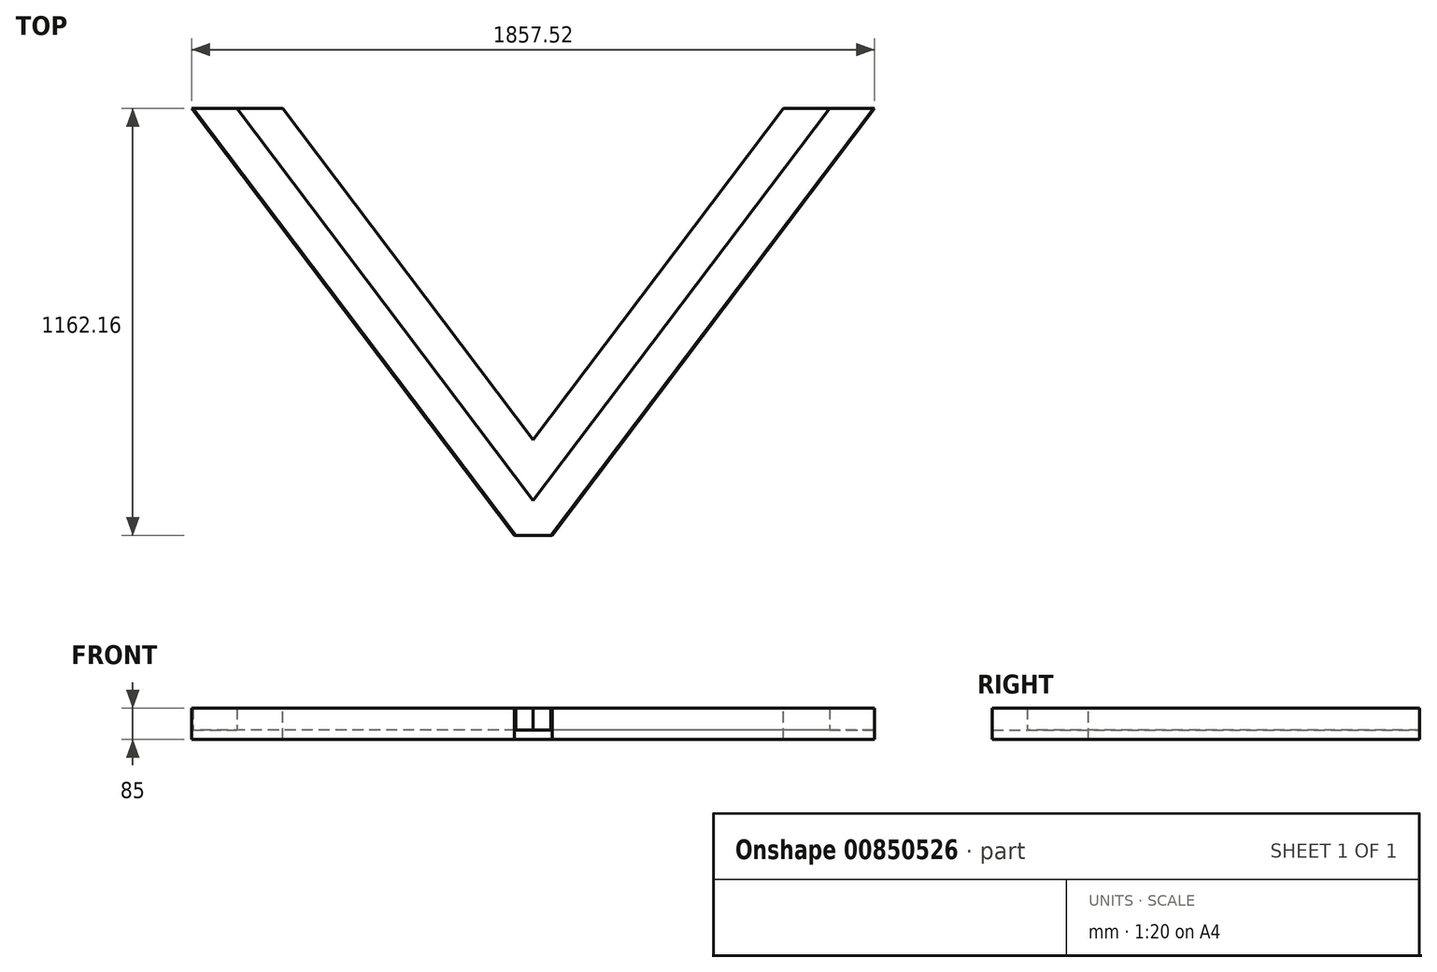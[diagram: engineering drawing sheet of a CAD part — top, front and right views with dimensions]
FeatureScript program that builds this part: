
annotation { "Feature Type Name" : "Feature", "Feature Type Description" : "" }
export const myFeature = defineFeature(function(context is Context, id is Id, definition is map)
    precondition{}
    {
        {
            var Q0;
            Q0=qCreatedBy(makeId("Top.planeOp"),FACE);
            var sketch = newSketch(context, id + "F0", { "sketchPlane" : qUnion([Q0])});
            skLineSegment(sketch, "E0", {"start": v(0, 0) * mm, "end": v(1850, 0) * mm});
            skLineSegment(sketch, "E1", {"start": v(1850, 0) * mm, "end": v(972.5, -1162.16) * mm});
            skPoint(sketch, "E1.endSnap0", {"position": v(925, 0) * mm});
            skLineSegment(sketch, "E2", {"start": v(877.5, -1162.16) * mm, "end": v(0, 0) * mm});
            skLineSegment(sketch, "E3", {"start": v(925, -1225.07) * mm, "end": v(925, -1010.6) * mm, "construction": true});
            skLineSegment(sketch, "E4", {"start": v(877.5, -1162.16) * mm, "end": v(972.5, -1162.16) * mm});
            skPoint(sketch, "E5.orphan", {"position": v(877.5, -1010.6) * mm});
            skPoint(sketch, "E6.orphan", {"position": v(972.5, -1010.6) * mm});
            skPoint(sketch, "E7.0.start.orphan", {"position": v(877.5, -1225.07) * mm});
            skPoint(sketch, "E8.MirrorCS.start.orphan", {"position": v(972.5, -1225.07) * mm});
            skSolve(sketch);
        }
        {
            var Q0;
            Q0=makeQuery(id+"F0.imprint","IMPRINT",FACE,{"disambiguationData":[TD([[makeQuery(id+"F0.imprint","IMPRINT",EDGE,{"derivedFrom":sQuery(id+"F0.wireOp",EDGE,"E0")}),-1.0]])]});
            extrude(context, id + "F1", {"entities" : qUnion([Q0]), "depth" : 25 * mm, "offsetDistance" : 25 * mm});
        }
        {
            var Q0;
            Q0=makeQuery(id+"F1.opExtrude","CAP_FACE",FACE,{"disambiguationData":[OSD([sQuery(id+"F0.wireOp",EDGE,"E0"),sQuery(id+"F0.wireOp",EDGE,"E1"),sQuery(id+"F0.wireOp",EDGE,"E2"),sQuery(id+"F0.wireOp",EDGE,"E4")])],"isStart":false});
            var sketch = newSketch(context, id + "F2", { "sketchPlane" : qUnion([Q0])});
            skLineSegment(sketch, "E9.0", {"start": v(925, -1067.42) * mm, "end": v(119.04, 0) * mm});
            skLineSegment(sketch, "E10.0", {"start": v(1730.96, 0) * mm, "end": v(925, -1067.42) * mm});
            skLineSegment(sketch, "E11", {"start": v(119.04, 0) * mm, "end": v(1730.96, 0) * mm});
            skSolve(sketch);
        }
        {
            var Q0;
            Q0=makeQuery(id+"F2.imprint","IMPRINT",FACE,{"disambiguationData":[TD([[makeQuery(id+"F2.imprint","IMPRINT",EDGE,{"derivedFrom":sQuery(id+"F2.wireOp",EDGE,"E9.0")}),-1.0]])]});
            extrude(context, id + "F3", {"entities" : qUnion([Q0]), "operationType" : NewBodyOperationType.ADD, "depth" : 60 * mm, "offsetDistance" : 25 * mm});
        }
        {
            var Q0;
            Q0=makeQuery(id+"F1.opExtrude","CAP_FACE",FACE,{"disambiguationData":[OSD([sQuery(id+"F0.wireOp",EDGE,"E0"),sQuery(id+"F0.wireOp",EDGE,"E1"),sQuery(id+"F0.wireOp",EDGE,"E2"),sQuery(id+"F0.wireOp",EDGE,"E4")])],"isStart":false});
            var sketch = newSketch(context, id + "F4", { "sketchPlane" : qUnion([Q0])});
            skLineSegment(sketch, "E12.0", {"start": v(873.74, -1162.16) * mm, "end": v(-3.76, 0) * mm});
            skLineSegment(sketch, "E13.0", {"start": v(1853.76, 0) * mm, "end": v(976.26, -1162.16) * mm});
            skLineSegment(sketch, "E14", {"start": v(0, 0) * mm, "end": v(-3.76, 0) * mm});
            skLineSegment(sketch, "E15", {"start": v(877.5, -1162.16) * mm, "end": v(873.74, -1162.16) * mm});
            skLineSegment(sketch, "E16", {"start": v(972.5, -1162.16) * mm, "end": v(976.26, -1162.16) * mm});
            skLineSegment(sketch, "E17", {"start": v(1850, 0) * mm, "end": v(1853.76, 0) * mm});
            skSolve(sketch);
        }
        {
            var Q0;
            Q0=makeQuery(id+"F4.imprint","IMPRINT",FACE,{"disambiguationData":[TD([[makeQuery(id+"F4.imprint","IMPRINT",EDGE,{"derivedFrom":sQuery(id+"F4.wireOp",EDGE,"E12.0")}),-1.0]])]});
            var Q1;
            Q1=makeQuery(id+"F4.imprint","IMPRINT",FACE,{"disambiguationData":[TD([[makeQuery(id+"F4.imprint","IMPRINT",EDGE,{"derivedFrom":sQuery(id+"F4.wireOp",EDGE,"E13.0")}),-1.0]])]});
            extrude(context, id + "F5", {"entities" : qUnion([Q0, Q1]), "operationType" : NewBodyOperationType.ADD, "depth" : 60 * mm, "offsetDistance" : 25 * mm, "hasSecondDirection" : true, "secondDirectionOppositeDirection" : true, "secondDirectionDepth" : 25 * mm});
        }
        {
            var Q0;
            Q0=makeQuery(id+"F3.opExtrude","CAP_FACE",FACE,{"disambiguationData":[OSD([sQuery(id+"F2.wireOp",EDGE,"E9.0"),sQuery(id+"F2.wireOp",EDGE,"E10.0"),sQuery(id+"F2.wireOp",EDGE,"E11")])],"isStart":false});
            var sketch = newSketch(context, id + "F6", { "sketchPlane" : qUnion([Q0])});
            skLineSegment(sketch, "E18.0", {"start": v(925, -901.46) * mm, "end": v(1605.66, 0) * mm});
            skLineSegment(sketch, "E18.1", {"start": v(244.34, 0) * mm, "end": v(925, -901.46) * mm});
            skLineSegment(sketch, "E19", {"start": v(244.34, 0) * mm, "end": v(1605.66, 0) * mm});
            skSolve(sketch);
        }
        {
            var Q0;
            Q0=makeQuery(id+"F6.imprint","IMPRINT",FACE,{"disambiguationData":[TD([[makeQuery(id+"F6.imprint","IMPRINT",EDGE,{"derivedFrom":sQuery(id+"F6.wireOp",EDGE,"E18.0")}),1.0]])]});
            extrude(context, id + "F7", {"entities" : qUnion([Q0]), "operationType" : NewBodyOperationType.REMOVE, "endBound" : BoundingType.THROUGH_ALL, "oppositeDirection" : true, "depth" : 25 * mm, "offsetDistance" : 25 * mm});
        }
    });
